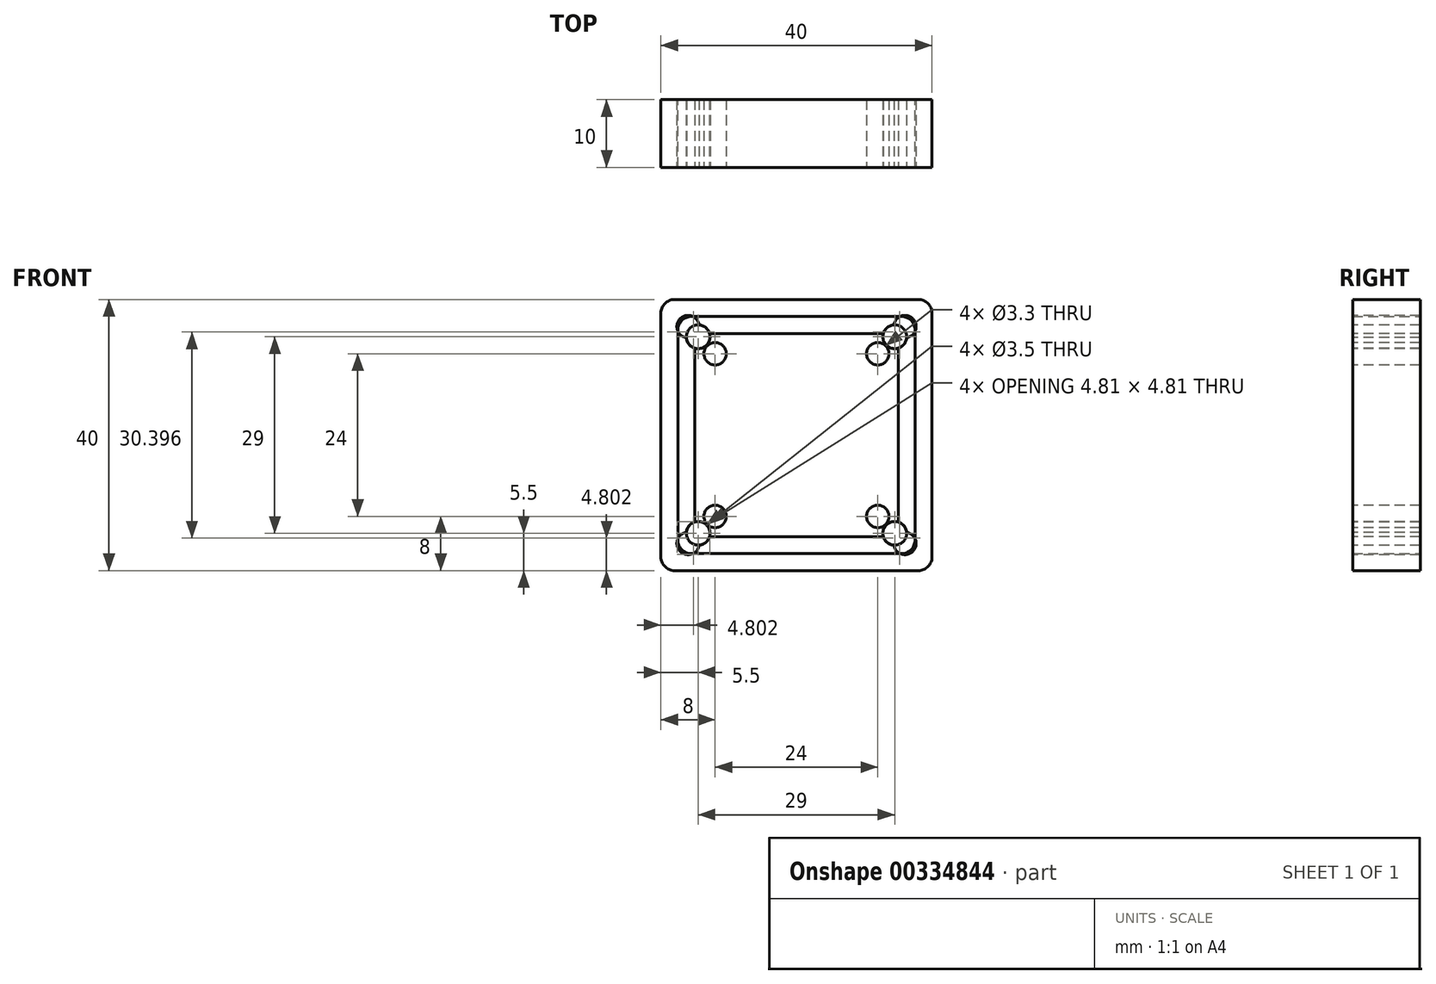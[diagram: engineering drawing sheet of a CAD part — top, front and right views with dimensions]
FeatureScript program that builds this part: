
annotation { "Feature Type Name" : "Feature", "Feature Type Description" : "" }
export const myFeature = defineFeature(function(context is Context, id is Id, definition is map)
    precondition{}
    {
        {
            var Q0;
            Q0=qCreatedBy(makeId("Front.planeOp"),FACE);
            var sketch = newSketch(context, id + "F0", { "sketchPlane" : qUnion([Q0])});
            skLineSegment(sketch, "E0.bottom", {"start": v(15, 15) * mm, "end": v(-15, 15) * mm});
            skLineSegment(sketch, "E0.top", {"start": v(15, -15) * mm, "end": v(-15, -15) * mm});
            skLineSegment(sketch, "E0.left", {"start": v(15, 15) * mm, "end": v(15, -15) * mm});
            skLineSegment(sketch, "E0.right", {"start": v(-15, 15) * mm, "end": v(-15, -15) * mm});
            skPoint(sketch, "E0.middle", {"position": v(0, 0) * mm});
            skSolve(sketch);
        }
        {
            var Q0;
            Q0 = qSketchRegion(id + "F0", true);
            extrude(context, id + "F1", {"entities" : qUnion([Q0]), "depth" : 10 * mm, "offsetDistance" : 25 * mm});
        }
        {
            var Q0;
            Q0=makeQuery(id+"F1.opExtrude","SWEPT_EDGE",EDGE,{"disambiguationData":[OSD([sQuery(id+"F0.wireOp",EDGE,"E0.bottom"),sQuery(id+"F0.wireOp",EDGE,"E0.right")])]});
            var Q1;
            Q1=makeQuery(id+"F1.opExtrude","SWEPT_EDGE",EDGE,{"disambiguationData":[OSD([sQuery(id+"F0.wireOp",EDGE,"E0.top"),sQuery(id+"F0.wireOp",EDGE,"E0.right")])]});
            var Q2;
            Q2=makeQuery(id+"F1.opExtrude","SWEPT_EDGE",EDGE,{"disambiguationData":[OSD([sQuery(id+"F0.wireOp",EDGE,"E0.top"),sQuery(id+"F0.wireOp",EDGE,"E0.left")])]});
            var Q3;
            Q3=makeQuery(id+"F1.opExtrude","SWEPT_EDGE",EDGE,{"disambiguationData":[OSD([sQuery(id+"F0.wireOp",EDGE,"E0.bottom"),sQuery(id+"F0.wireOp",EDGE,"E0.left")])]});
            fillet(context, id + "F2", {"entities" : qUnion([Q0, Q1, Q2, Q3]), "tangentPropagation" : true, "radius" : 2 * mm, "defaultsChanged" : false, "vertexSettings" : [], "allowEdgeOverflow" : false});
        }
        {
            var Q0;
            Q0=makeQuery(id+"F1.opExtrude","CAP_FACE",FACE,{"disambiguationData":[OSD([sQuery(id+"F0.wireOp",EDGE,"E0.bottom"),sQuery(id+"F0.wireOp",EDGE,"E0.top"),sQuery(id+"F0.wireOp",EDGE,"E0.left"),sQuery(id+"F0.wireOp",EDGE,"E0.right")])],"isStart":false});
            var sketch = newSketch(context, id + "F3", { "sketchPlane" : qUnion([Q0])});
            skCircle(sketch, "E1", {"center": v(-12, 12) * mm, "radius": 1.65 * mm});
            skLineSegment(sketch, "E2", {"start": v(0, 9.81) * mm, "end": v(0, 0) * mm, "construction": true});
            skLineSegment(sketch, "E3", {"start": v(0, 0) * mm, "end": v(8.15, 0) * mm, "construction": true});
            skCircle(sketch, "E4.MirrorC", {"center": v(12, 12) * mm, "radius": 1.65 * mm});
            skCircle(sketch, "E5.MirrorC", {"center": v(12, -12) * mm, "radius": 1.65 * mm});
            skCircle(sketch, "E6.MirrorC", {"center": v(-12, -12) * mm, "radius": 1.65 * mm});
            skSolve(sketch);
        }
        {
            var Q0;
            Q0 = qSketchRegion(id + "F3", true);
            extrude(context, id + "F4", {"entities" : qUnion([Q0]), "operationType" : NewBodyOperationType.REMOVE, "oppositeDirection" : true, "depth" : 25 * mm, "offsetDistance" : 25 * mm});
        }
        {
            var Q0;
            Q0=qCreatedBy(makeId("Front.planeOp"),FACE);
            var sketch = newSketch(context, id + "F5", { "sketchPlane" : qUnion([Q0])});
            skLineSegment(sketch, "E7.bottom", {"start": v(20, 20) * mm, "end": v(-20, 20) * mm});
            skLineSegment(sketch, "E7.top", {"start": v(20, -20) * mm, "end": v(-20, -20) * mm});
            skLineSegment(sketch, "E7.left", {"start": v(20, 20) * mm, "end": v(20, -20) * mm});
            skLineSegment(sketch, "E7.right", {"start": v(-20, 20) * mm, "end": v(-20, -20) * mm});
            skPoint(sketch, "E7.middle", {"position": v(0, 0) * mm});
            skSolve(sketch);
        }
        {
            var Q0;
            Q0 = qSketchRegion(id + "F5", true);
            extrude(context, id + "F6", {"entities" : qUnion([Q0]), "depth" : 10 * mm, "offsetDistance" : 25 * mm});
        }
        {
            var Q0;
            Q0=makeQuery(id+"F6.opExtrude","SWEPT_EDGE",EDGE,{"disambiguationData":[OSD([sQuery(id+"F5.wireOp",EDGE,"E7.bottom"),sQuery(id+"F5.wireOp",EDGE,"E7.right")])]});
            var Q1;
            Q1=makeQuery(id+"F6.opExtrude","SWEPT_EDGE",EDGE,{"disambiguationData":[OSD([sQuery(id+"F5.wireOp",EDGE,"E7.top"),sQuery(id+"F5.wireOp",EDGE,"E7.right")])]});
            var Q2;
            Q2=makeQuery(id+"F6.opExtrude","SWEPT_EDGE",EDGE,{"disambiguationData":[OSD([sQuery(id+"F5.wireOp",EDGE,"E7.bottom"),sQuery(id+"F5.wireOp",EDGE,"E7.left")])]});
            var Q3;
            Q3=makeQuery(id+"F6.opExtrude","SWEPT_EDGE",EDGE,{"disambiguationData":[OSD([sQuery(id+"F5.wireOp",EDGE,"E7.top"),sQuery(id+"F5.wireOp",EDGE,"E7.left")])]});
            fillet(context, id + "F7", {"entities" : qUnion([Q0, Q1, Q2, Q3]), "tangentPropagation" : true, "radius" : 2 * mm, "defaultsChanged" : false, "vertexSettings" : [], "allowEdgeOverflow" : false});
        }
        {
            var Q0;
            Q0=makeQuery(id+"F6.opExtrude","CAP_FACE",FACE,{"disambiguationData":[OSD([sQuery(id+"F5.wireOp",EDGE,"E7.bottom"),sQuery(id+"F5.wireOp",EDGE,"E7.top"),sQuery(id+"F5.wireOp",EDGE,"E7.left"),sQuery(id+"F5.wireOp",EDGE,"E7.right")])],"isStart":false});
            var sketch = newSketch(context, id + "F8", { "sketchPlane" : qUnion([Q0])});
            skCircle(sketch, "E8", {"center": v(-16, 16) * mm, "radius": 1.65 * mm});
            skLineSegment(sketch, "E9", {"start": v(0, 8.95) * mm, "end": v(0, 0) * mm, "construction": true});
            skLineSegment(sketch, "E10", {"start": v(0, 0) * mm, "end": v(8.48, 0) * mm, "construction": true});
            skCircle(sketch, "E11.MirrorC", {"center": v(16, 16) * mm, "radius": 1.65 * mm});
            skCircle(sketch, "E12.MirrorC", {"center": v(-16, -16) * mm, "radius": 1.65 * mm});
            skCircle(sketch, "E13.MirrorC", {"center": v(16, -16) * mm, "radius": 1.65 * mm});
            skSolve(sketch);
        }
        {
            var Q0;
            Q0 = qSketchRegion(id + "F8", true);
            extrude(context, id + "F9", {"entities" : qUnion([Q0]), "operationType" : NewBodyOperationType.REMOVE, "oppositeDirection" : true, "depth" : 25 * mm, "offsetDistance" : 25 * mm});
        }
        {
            var Q0;
            Q0=qCreatedBy(makeId("Front.planeOp"),FACE);
            var sketch = newSketch(context, id + "F10", { "sketchPlane" : qUnion([Q0])});
            skLineSegment(sketch, "E14.bottom", {"start": v(17.5, 17.5) * mm, "end": v(-17.5, 17.5) * mm});
            skLineSegment(sketch, "E14.top", {"start": v(17.5, -17.5) * mm, "end": v(-17.5, -17.5) * mm});
            skLineSegment(sketch, "E14.left", {"start": v(17.5, 17.5) * mm, "end": v(17.5, -17.5) * mm});
            skLineSegment(sketch, "E14.right", {"start": v(-17.5, 17.5) * mm, "end": v(-17.5, -17.5) * mm});
            skPoint(sketch, "E14.middle", {"position": v(0, 0) * mm});
            skSolve(sketch);
        }
        {
            var Q0;
            Q0 = qSketchRegion(id + "F10", true);
            extrude(context, id + "F11", {"entities" : qUnion([Q0]), "depth" : 10 * mm, "offsetDistance" : 25 * mm});
        }
        {
            var Q0;
            Q0=makeQuery(id+"F11.opExtrude","SWEPT_EDGE",EDGE,{"disambiguationData":[OSD([sQuery(id+"F10.wireOp",EDGE,"E14.bottom"),sQuery(id+"F10.wireOp",EDGE,"E14.right")])]});
            var Q1;
            Q1=makeQuery(id+"F11.opExtrude","SWEPT_EDGE",EDGE,{"disambiguationData":[OSD([sQuery(id+"F10.wireOp",EDGE,"E14.top"),sQuery(id+"F10.wireOp",EDGE,"E14.right")])]});
            var Q2;
            Q2=makeQuery(id+"F11.opExtrude","SWEPT_EDGE",EDGE,{"disambiguationData":[OSD([sQuery(id+"F10.wireOp",EDGE,"E14.bottom"),sQuery(id+"F10.wireOp",EDGE,"E14.left")])]});
            var Q3;
            Q3=makeQuery(id+"F11.opExtrude","SWEPT_EDGE",EDGE,{"disambiguationData":[OSD([sQuery(id+"F10.wireOp",EDGE,"E14.top"),sQuery(id+"F10.wireOp",EDGE,"E14.left")])]});
            fillet(context, id + "F12", {"entities" : qUnion([Q0, Q1, Q2, Q3]), "tangentPropagation" : true, "radius" : 2 * mm, "defaultsChanged" : false, "vertexSettings" : [], "allowEdgeOverflow" : false});
        }
        {
            var Q0;
            Q0=makeQuery(id+"F11.opExtrude","CAP_FACE",FACE,{"disambiguationData":[OSD([sQuery(id+"F10.wireOp",EDGE,"E14.bottom"),sQuery(id+"F10.wireOp",EDGE,"E14.top"),sQuery(id+"F10.wireOp",EDGE,"E14.left"),sQuery(id+"F10.wireOp",EDGE,"E14.right")])],"isStart":false});
            var sketch = newSketch(context, id + "F13", { "sketchPlane" : qUnion([Q0])});
            skCircle(sketch, "E15", {"center": v(-14.5, 14.5) * mm, "radius": 1.75 * mm});
            skLineSegment(sketch, "E16", {"start": v(0, 7.1) * mm, "end": v(0, 0) * mm, "construction": true});
            skLineSegment(sketch, "E17", {"start": v(0, 0) * mm, "end": v(7.33, 0) * mm, "construction": true});
            skCircle(sketch, "E18.MirrorC", {"center": v(14.5, 14.5) * mm, "radius": 1.75 * mm});
            skCircle(sketch, "E19.MirrorC", {"center": v(14.5, -14.5) * mm, "radius": 1.75 * mm});
            skCircle(sketch, "E20.MirrorC", {"center": v(-14.5, -14.5) * mm, "radius": 1.75 * mm});
            skSolve(sketch);
        }
        {
            var Q0;
            Q0 = qSketchRegion(id + "F13", true);
            extrude(context, id + "F14", {"entities" : qUnion([Q0]), "operationType" : NewBodyOperationType.REMOVE, "oppositeDirection" : true, "depth" : 25 * mm, "offsetDistance" : 25 * mm});
        }
    });
